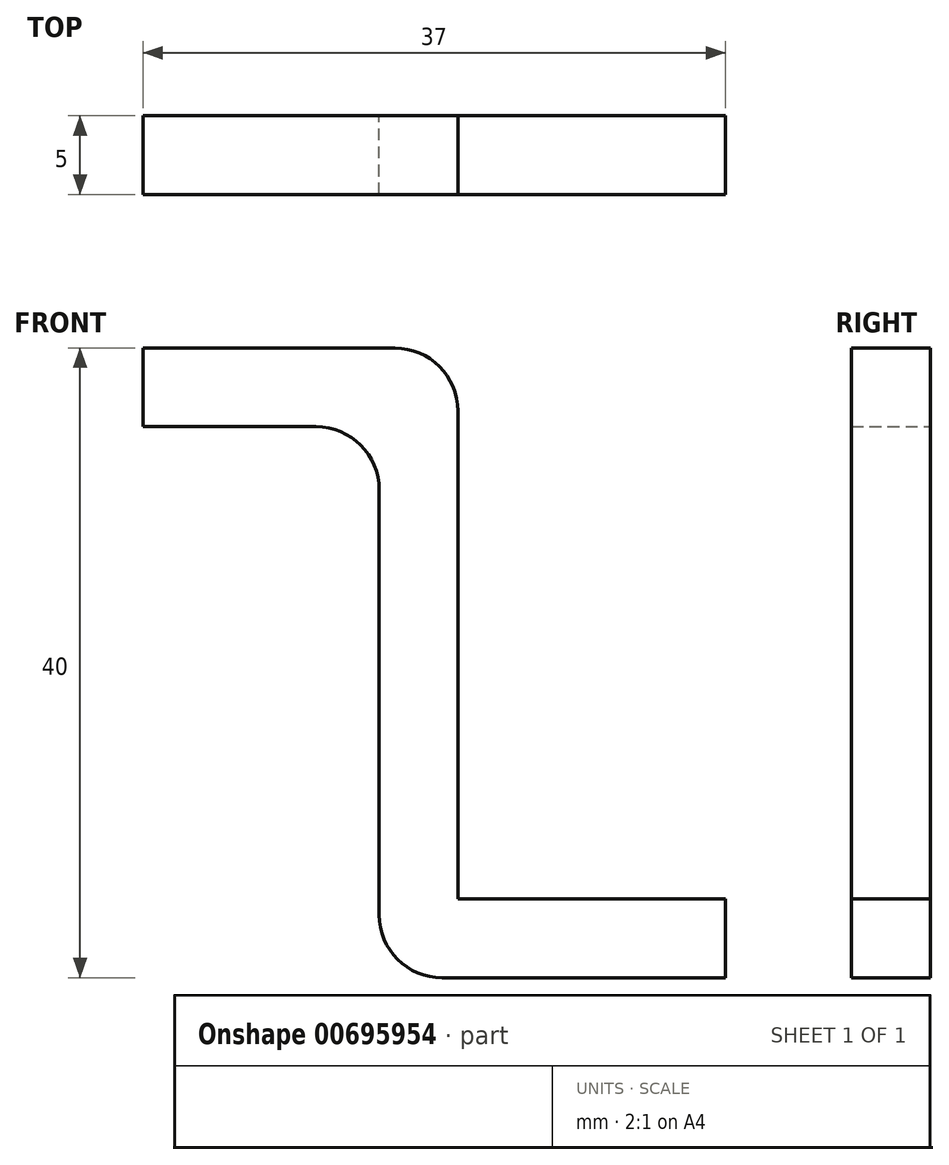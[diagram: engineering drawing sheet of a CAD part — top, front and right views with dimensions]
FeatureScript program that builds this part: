
annotation { "Feature Type Name" : "Feature", "Feature Type Description" : "" }
export const myFeature = defineFeature(function(context is Context, id is Id, definition is map)
    precondition{}
    {
        {
            var Q0;
            Q0=qCreatedBy(makeId("Front.planeOp"),FACE);
            var sketch = newSketch(context, id + "F0", { "sketchPlane" : qUnion([Q0])});
            skLineSegment(sketch, "E0", {"start": v(-26.14, 24.6) * mm, "end": v(-15.14, 24.6) * mm});
            skLineSegment(sketch, "E1", {"start": v(-11.14, 20.6) * mm, "end": v(-11.14, -6.4) * mm});
            skLineSegment(sketch, "E2", {"start": v(-7.14, -10.4) * mm, "end": v(10.86, -10.4) * mm});
            skLineSegment(sketch, "E3", {"start": v(10.86, -10.4) * mm, "end": v(10.86, -5.4) * mm});
            skLineSegment(sketch, "E4", {"start": v(10.86, -5.4) * mm, "end": v(-6.14, -5.4) * mm});
            skLineSegment(sketch, "E5", {"start": v(-6.14, -5.4) * mm, "end": v(-6.14, 25.6) * mm});
            skLineSegment(sketch, "E6", {"start": v(-10.14, 29.6) * mm, "end": v(-26.14, 29.6) * mm});
            skLineSegment(sketch, "E7", {"start": v(-26.14, 29.6) * mm, "end": v(-26.14, 24.6) * mm});
            skPoint(sketch, "E8.visualSharp", {"position": v(-6.14, 29.6) * mm});
            skArc(sketch, "E8.filletArc", {"start": v(-6.14, 25.6) * mm, "mid": v(-7.31, 28.44) * mm, "end": v(-10.14, 29.6) * mm});
            skPoint(sketch, "E9.visualSharp", {"position": v(-11.14, 24.6) * mm});
            skArc(sketch, "E9.filletArc", {"start": v(-11.14, 20.6) * mm, "mid": v(-12.31, 23.44) * mm, "end": v(-15.14, 24.6) * mm});
            skPoint(sketch, "E10.visualSharp", {"position": v(-11.14, -10.4) * mm});
            skArc(sketch, "E10.filletArc", {"start": v(-11.14, -6.4) * mm, "mid": v(-9.97, -9.22) * mm, "end": v(-7.14, -10.4) * mm});
            skSolve(sketch);
        }
        {
            var Q0;
            Q0=makeQuery(id+"F0.imprint","IMPRINT",FACE,{"disambiguationData":[TD([[makeQuery(id+"F0.imprint","IMPRINT",EDGE,{"derivedFrom":sQuery(id+"F0.wireOp",EDGE,"E0")}),1.0]])]});
            extrude(context, id + "F1", {"entities" : qUnion([Q0]), "depth" : 5 * mm, "offsetDistance" : 25 * mm});
        }
    });
